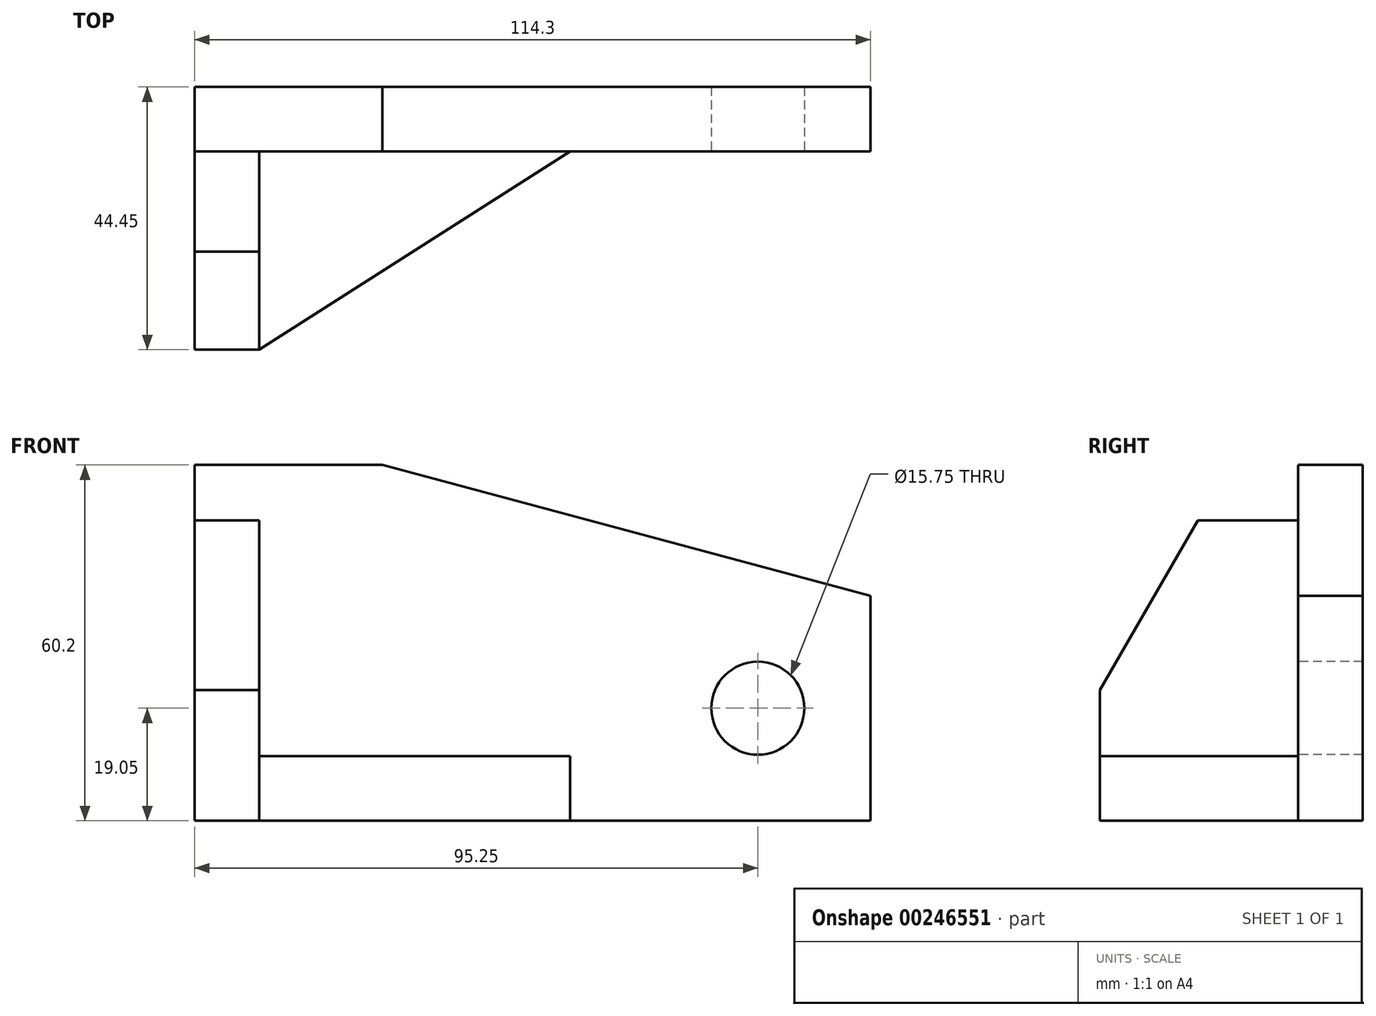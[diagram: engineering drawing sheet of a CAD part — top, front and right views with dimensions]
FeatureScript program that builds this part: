
annotation { "Feature Type Name" : "Feature", "Feature Type Description" : "" }
export const myFeature = defineFeature(function(context is Context, id is Id, definition is map)
    precondition{}
    {
        {
            var Q0;
            Q0=qCreatedBy(makeId("Top.planeOp"),FACE);
            var sketch = newSketch(context, id + "F0", { "sketchPlane" : qUnion([Q0])});
            skLineSegment(sketch, "E0.bottom", {"start": v(-66.7, -22.79) * mm, "end": v(47.6, -22.79) * mm});
            skLineSegment(sketch, "E0.top", {"start": v(-66.7, -11.87) * mm, "end": v(47.6, -11.87) * mm});
            skLineSegment(sketch, "E0.left", {"start": v(-66.7, -22.79) * mm, "end": v(-66.7, -11.87) * mm});
            skLineSegment(sketch, "E0.right", {"start": v(47.6, -22.79) * mm, "end": v(47.6, -11.87) * mm});
            skPoint(sketch, "E1", {"position": v(-66.7, -22.79) * mm});
            skSolve(sketch);
        }
        {
            var Q0;
            Q0=qCreatedBy(makeId("Top.planeOp"),FACE);
            var sketch = newSketch(context, id + "F1", { "sketchPlane" : qUnion([Q0])});
            skPoint(sketch, "E2.0", {"position": v(-66.7, -22.79) * mm});
            skLineSegment(sketch, "E3.bottom", {"start": v(-66.7, -22.79) * mm, "end": v(-3.2, -22.79) * mm});
            skLineSegment(sketch, "E3.top", {"start": v(-66.7, -56.32) * mm, "end": v(-3.2, -56.32) * mm});
            skLineSegment(sketch, "E3.left", {"start": v(-66.7, -22.79) * mm, "end": v(-66.7, -56.32) * mm});
            skLineSegment(sketch, "E3.right", {"start": v(-3.2, -22.79) * mm, "end": v(-3.2, -56.32) * mm});
            skSolve(sketch);
        }
        {
            var Q0;
            Q0 = qSketchRegion(id + "F0", true);
            extrude(context, id + "F2", {"entities" : qUnion([Q0]), "depth" : 60.2 * mm});
        }
        {
            var Q0;
            Q0=makeQuery(id+"F2.opExtrude","CAP_EDGE",EDGE,{"disambiguationData":[OSD([sQuery(id+"F0.wireOp",EDGE,"E0.right")])],"isStart":false});
            chamfer(context, id + "F3", {"entities" : qUnion([Q0]), "chamferType" : ChamferType.OFFSET_ANGLE, "width" : 82.55 * mm, "oppositeDirection" : false, "angle" : 15 * degree, "tangentPropagation" : true});
        }
        {
            var Q0;
            Q0=makeQuery(id+"F1.imprint","IMPRINT",FACE,{"disambiguationData":[TD([[makeQuery(id+"F1.imprint","IMPRINT",EDGE,{"derivedFrom":sQuery(id+"F1.wireOp",EDGE,"E3.bottom")}),-1.0]])]});
            var sketch = newSketch(context, id + "F4", { "sketchPlane" : qUnion([Q0])});
            skLineSegment(sketch, "E4.0", {"start": v(-66.7, -22.79) * mm, "end": v(-66.7, -56.32) * mm});
            skLineSegment(sketch, "E4.1", {"start": v(-66.7, -22.79) * mm, "end": v(-3.2, -22.79) * mm});
            skLineSegment(sketch, "E4.2", {"start": v(-66.7, -56.32) * mm, "end": v(-3.2, -56.32) * mm});
            skLineSegment(sketch, "E5", {"start": v(-55.79, -22.79) * mm, "end": v(-55.79, -56.32) * mm});
            skSolve(sketch);
        }
        {
            var Q0;
            {var subQ0=sQuery(id+"F4.wireOp",EDGE,"E4.0");Q0=makeQuery(id+"F4.imprint","IMPRINT",FACE,{"disambiguationData":[TD([[makeQuery(id+"F4.imprint","IMPRINT",EDGE,{"derivedFrom":subQ0}),1.0]])]});}
            extrude(context, id + "F5", {"entities" : qUnion([Q0]), "operationType" : NewBodyOperationType.ADD, "depth" : 50.8 * mm});
        }
        {
            var Q0;
            Q0=makeQuery(id+"F2.opExtrude","SWEPT_FACE",FACE,{"disambiguationData":[OSD([sQuery(id+"F0.wireOp",EDGE,"E0.bottom")])]});
            var sketch = newSketch(context, id + "F6", { "sketchPlane" : qUnion([Q0])});
            skPoint(sketch, "E6", {"position": v(-55.79, 50.8) * mm});
            skSolve(sketch);
        }
        {
            var Q0;
            {var subQ0=sQuery(id+"FABFoki6c4oKF2w_1.wireOp",EDGE,"dxGwiZxE-U0Cg-JMQu-BHJq-477hJAI4Fc4m");Q0=makeQuery(id+"FABFoki6c4oKF2w_1.imprint","IMPRINT",FACE,{"disambiguationData":[TD([[makeQuery(id+"FABFoki6c4oKF2w_1.imprint","IMPRINT",EDGE,{"derivedFrom":subQ0}),-1.0]])]});}
            var sketch = newSketch(context, id + "F7", { "sketchPlane" : qUnion([Q0])});
            skLineSegment(sketch, "E7.0", {"start": v(-66.7, 22.1) * mm, "end": v(-55.79, 22.1) * mm});
            skSolve(sketch);
        }
        {
            var Q0;
            Q0=makeQuery(id+"F5.opExtrude","SWEPT_FACE",FACE,{"disambiguationData":[OSD([sQuery(id+"F4.wireOp",EDGE,"E5")])]});
            var sketch = newSketch(context, id + "F8", { "sketchPlane" : qUnion([Q0])});
            skLineSegment(sketch, "E8.0", {"start": v(-56.32, 50.8) * mm, "end": v(-39.75, 50.8) * mm});
            skPoint(sketch, "E9.0", {"position": v(-56.32, 22.1) * mm});
            skLineSegment(sketch, "E10", {"start": v(-39.75, 50.8) * mm, "end": v(-56.32, 22.1) * mm});
            skSolve(sketch);
        }
        {
            var Q0;
            {var subQ0=sQuery(id+"F8.wireOp",EDGE,"E8.0");Q0=makeQuery(id+"F8.imprint","IMPRINT",FACE,{"disambiguationData":[TD([[makeQuery(id+"F8.imprint","IMPRINT",EDGE,{"derivedFrom":subQ0}),1.0]])]});}
            extrude(context, id + "F9", {"entities" : qUnion([Q0]), "operationType" : NewBodyOperationType.REMOVE, "oppositeDirection" : true, "depth" : 40.4 * mm});
        }
        {
            var Q0;
            Q0=makeQuery(id+"F1.imprint","IMPRINT",FACE,{"disambiguationData":[TD([[makeQuery(id+"F1.imprint","IMPRINT",EDGE,{"derivedFrom":sQuery(id+"F1.wireOp",EDGE,"E3.bottom")}),-1.0]])]});
            var sketch = newSketch(context, id + "F10", { "sketchPlane" : qUnion([Q0])});
            skLineSegment(sketch, "E11.1", {"start": v(-55.79, -22.79) * mm, "end": v(-55.79, -56.32) * mm});
            skPoint(sketch, "E12.0", {"position": v(-3.2, -22.79) * mm});
            skLineSegment(sketch, "E13", {"start": v(-55.79, -56.32) * mm, "end": v(-3.2, -22.79) * mm});
            skSolve(sketch);
        }
        {
            var Q0;
            {var subQ0=sQuery(id+"F10.wireOp",EDGE,"E11.1");Q0=makeQuery(id+"F10.imprint","IMPRINT",FACE,{"disambiguationData":[TD([[makeQuery(id+"F10.imprint","IMPRINT",EDGE,{"derivedFrom":subQ0}),1.0]])]});}
            extrude(context, id + "F11", {"entities" : qUnion([Q0]), "operationType" : NewBodyOperationType.ADD, "depth" : 10.92 * mm});
        }
        {
            var Q0;
            {var subQ0=sQuery(id+"F0.wireOp",EDGE,"E0.bottom");Q0=makeQuery(id+"F6.imprint","IMPRINT",FACE,{"disambiguationData":[TD([[makeQuery(id+"F6.imprint","IMPRINT",EDGE,{"derivedFrom":makeQuery(id+"F2.opExtrude","CAP_EDGE",EDGE,{"disambiguationData":[OSD([subQ0])],"isStart":false})}),-1.0]])]});}
            var sketch = newSketch(context, id + "F12", { "sketchPlane" : qUnion([Q0])});
            skPoint(sketch, "E14.0", {"position": v(47.6, 0) * mm});
            skLineSegment(sketch, "E15.bottom", {"start": v(47.6, 0) * mm, "end": v(28.54, 0) * mm});
            skLineSegment(sketch, "E15.top", {"start": v(47.6, 19.05) * mm, "end": v(28.54, 19.05) * mm});
            skLineSegment(sketch, "E15.left", {"start": v(47.6, 0) * mm, "end": v(47.6, 19.05) * mm});
            skLineSegment(sketch, "E15.right", {"start": v(28.54, 0) * mm, "end": v(28.54, 19.05) * mm});
            skSolve(sketch);
        }
        {
            var Q0;
            Q0=sQuery(id+"F12.wireOp",VERTEX,"E15.top.end");
            var Q1;
            Q1=makeQuery(id+"F2.opExtrude","SWEPT_BODY",BODY,{"disambiguationData":[OSD([sQuery(id+"F0.wireOp",EDGE,"E0.bottom"),sQuery(id+"F0.wireOp",EDGE,"E0.top"),sQuery(id+"F0.wireOp",EDGE,"E0.left"),sQuery(id+"F0.wireOp",EDGE,"E0.right")])]});
            hole(context, id + "F13", {"style" : HoleStyle.SIMPLE, "endStyle" : HoleEndStyle.THROUGH, "holeDiameter" : 15.75 * mm, "tappedDepth" : 12.7 * mm, "tapClearance" : 3, "locations" : qUnion([Q0]), "scope" : qUnion([Q1])});
        }
    });
